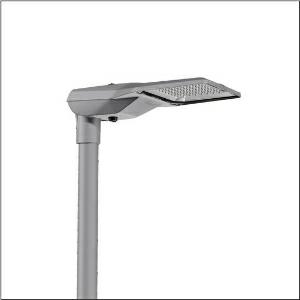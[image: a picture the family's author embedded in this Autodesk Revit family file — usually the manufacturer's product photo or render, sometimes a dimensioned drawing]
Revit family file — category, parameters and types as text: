
# Revit family: streetlight_sl_21_iq_midi___st1_0a_5xe3d51y08mb_fe0f
name_source: partatom
category: Lighting Fixtures
units: mm (PartAtom-declared; Revit-internal decimal feet)

## family parameters
Cut with Voids When Loaded = No
Host = Face
Light Source = No
Part Type = Normal
Room Calculation Point = No
Round Connector Dimension = Use Diameter
Shared = No

## types (1)
- --- (1 x LED, 16100 lm, 129.3 W, 3000K)
    Apparent Load = 129 VA
    CIE Flux Codes = 37 72 97 100 100
    Color Rendering = 80
    Color Temperature = 3000K
    Default Elevation = 1800 mm
    Description = Streetlight SL 21 iQ midi, mast luminaire, primary light control with lens, of PMMA, primary optical cover: cover, of toughened safety glass, transparent, light distribution: ST1.0a, light emission: direct distribution, primary light characteristic: asymmetric, installation type: post-top, side-entry, LED, High Power LED, rated luminous flux: 16.100lm, luminous efficacy: 125lm/W, light colour: 830, colour temperature: 3000K, control gear: iQ-Street Remote, D4i with power reduction, control: pre-setting: logarithmic dimming characteristic, Street-Remote, Auto-Match, Temp-Guard, Lumen-Switch, Night-Set, Smart-Wire, Light-Fading, Desk-Remote (wireless, voltage-free reading and setting of iQ features in the workshop via application-optimized NFC function/RFID function), optimised constant luminous flux control (CLO 2.0), mains connection: 230..240V, AC, 50/60Hz, start of lifetime: 129W, end of service life: 142W, reduction: 56W, luminaire housing, of diecast aluminium, powder-coated, Siteco® metallic grey (DB 702S), corrosivity category C5 mid according to DIN EN ISO 12944, please order mast flange separately, inclination adjustable: 0°, 5°, 10°, 15°, sealing non-destructively replaceable, multi-level sealing system, length: 644mm, width: 335mm, height: 110mm, mast flange for spigot size: 42mm (side-entry): 5XC10008XM4, 60/48mm (side-entry/post-top): 5XC10108XM2, 76/60mm (side-entry/post-top): 5XC10108XM1, mounting height: 4..8m, Smart Interface below and above, protection rating (complete): IP66, insulation class (complete): insulation class II (safety insulation), certification: CE, ENEC, ENEC+, VDE, impact resistance: IK10, permissible operating ambient temperature for outdoor applications: -40..+50°C, standard-compliant lighting for roads and squares, packaging unit: 1 piece

Light Distribution: ST1.0a
    Height = 111 mm
    Lamp = 1 x LED
    Lamp Light Flux = 16100 lm
    Lamp Power = 129.3 W
    Lamp count = 1
    Length = 644 mm
    Luminous efficacy = 125 lm/W
    Manufacturer = Siteco
    ModVariant = No
    Model = 5XE3D51Y08MB
    Number of Poles = 1
    OnlyDefault = Yes
    Power Factor = 1
    Product Name = Streetlight SL 21 iQ midi | ST1.0a
    Product group = mast luminaire | pylon top
    ProductGroupID = 6100
    Protection Class = Protection class II
    Protection Degree = IP 66
    RLX_Detail_Level = 1
    RLX_Emergency_Light_Flux = 0 lm
    RLX_Emergency_Type = 0
    RLX_Emergency_Type_DB = No
    RlxData = <blob elided: 90889 chars, md5=9d72b088>
    Socket = socket
    Standby Power = 0 W
    System Light Flux = 16100 lm
    System Power = 129 W
    Type Comments = factory setting: luminous flux: 100 % | dim-lin: 254 | 672 mA
    Type Image = l_1004304.jpg
    URL = http://relux.com
    VarID = @adj_135969
    Voltage = 0 V
    Weight = 0.00 kg
    Width = 336 mm

## geometry (parser evidence)
native form markers: Blend x4, Sweep x10
no freeform markers — native parametric forms only
